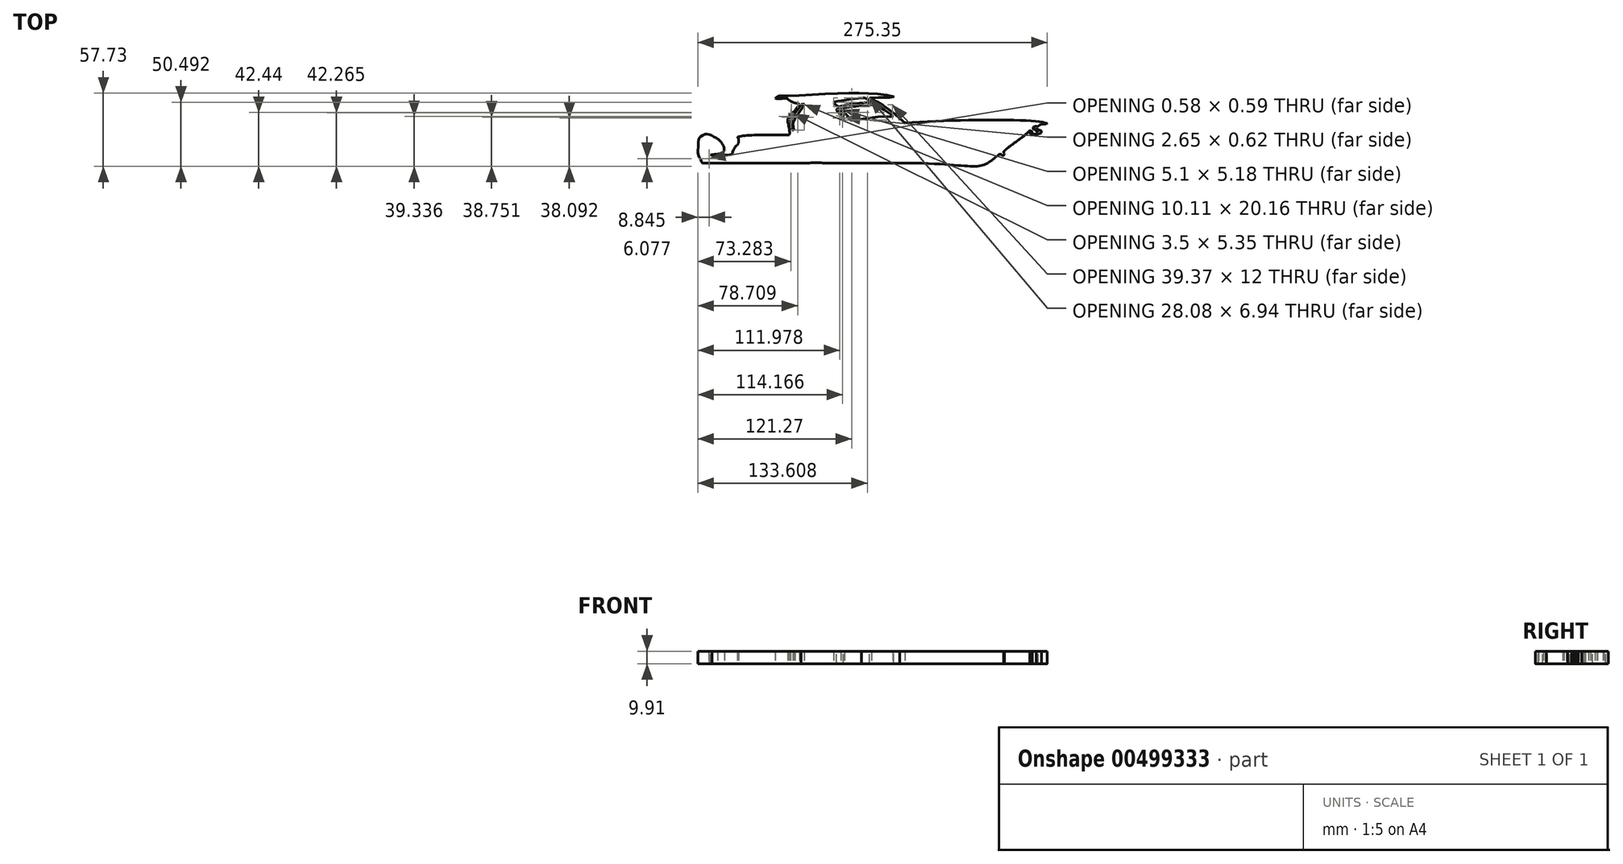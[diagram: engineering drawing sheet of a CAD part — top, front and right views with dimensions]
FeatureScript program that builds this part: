
annotation { "Feature Type Name" : "Feature", "Feature Type Description" : "" }
export const myFeature = defineFeature(function(context is Context, id is Id, definition is map)
    precondition{}
    {
        {
            var Q0;
            Q0=qCreatedBy(makeId("Top.planeOp"),FACE);
            var sketch = newSketch(context, id + "F0", { "sketchPlane" : qUnion([Q0])});
            skFitSpline(sketch, "E0", {"points": [v(181.82, 12.96) * mm, v(177.4, 14.1) * mm, v(69.7, 13.5) * mm, v(25.53, 9.3) * mm, v(19.92, 8.52) * mm], "startDerivative": vector(1.7, -4.6) * mm, "endDerivative": vector(-96.1, -9.77) * mm});
            skFitSpline(sketch, "E1", {"points": [v(19.92, 8.52) * mm, v(11.89, 7.3) * mm, v(0, 4.75) * mm, v(-5.76, 3.64) * mm, v(-21.62, 3.73) * mm, v(-57.86, 3.13) * mm, v(-62.13, 1.85) * mm, v(-60.42, 1.34) * mm, v(-58.8, 1) * mm, v(-52.92, 0.83) * mm, v(-44.65, 0.83) * mm, v(-38.6, 0.91) * mm, v(-28.44, 1) * mm, v(-16.08, 0.83) * mm, v(-10.37, 0.91) * mm, v(-5.5, 0.91) * mm, v(-2.78, 1.42) * mm, v(1.49, 2.79) * mm, v(4.56, 3.64) * mm, v(10.7, 4.66) * mm, v(15.39, 5.6) * mm, v(20.67, 6.46) * mm, v(27.84, 7.48) * mm, v(53.16, 10.3) * mm, v(65.53, 10.8) * mm, v(70.56, 11.23) * mm, v(181.82, 12.96) * mm], "startDerivative": vector(-204.32, -26.46) * mm, "endDerivative": vector(1116.59, 11.05) * mm});
            skFitSpline(sketch, "E2", {"points": [v(150.8, -6.4) * mm, v(136.83, -7.24) * mm, v(77, -11.4) * mm, v(39.07, -13.62) * mm, v(-5.53, -13.97) * mm, v(-32.22, -13.7) * mm, v(-56.7, -13.54) * mm, v(-83.8, -13.7) * mm, v(-84.92, -14.48) * mm, v(-83.04, -15.59) * mm, v(-76.47, -15.59) * mm, v(-57.71, -15.59) * mm, v(-38.53, -16.01) * mm, v(-32.64, -16.01) * mm, v(-7.32, -16.01) * mm, v(12.55, -15.84) * mm, v(72.24, -13.54) * mm, v(94.33, -11.75) * mm, v(106.35, -10.81) * mm, v(150.8, -6.4) * mm]});
            skFitSpline(sketch, "E3", {"points": [v(-62.13, 1.85) * mm, v(-61.49, 0.78) * mm, v(-61.61, -2.84) * mm, v(-63.48, -5.07) * mm, v(-65.9, -9.53) * mm, v(-67.22, -11.64) * mm, v(-83.62, -12) * mm, v(-83.38, -12.3) * mm, v(-83.8, -13.7) * mm], "startDerivative": vector(9.33, -10.43) * mm, "endDerivative": vector(-10.89, -19.72) * mm});
            skFitSpline(sketch, "E4", {"points": [v(-83.62, -12) * mm, v(-73.3, -9.4) * mm, v(-74.45, -2.78) * mm, v(-77.88, 0.76) * mm], "startDerivative": vector(4.15, 3.72) * mm, "endDerivative": vector(-20.22, 12.96) * mm});
            skFitSpline(sketch, "E5", {"points": [v(-77.88, 0.76) * mm, v(-79.82, 1.87) * mm, v(-83.38, 3.86) * mm, v(-86.1, 4.58) * mm, v(-88.98, 3.98) * mm, v(-91.58, 2.29) * mm, v(-92.7, 0.76) * mm, v(-92.95, -2.8) * mm, v(-93.16, -6.9) * mm, v(-93.43, -10.58) * mm, v(-92.18, -13.75) * mm, v(-90.43, -17.3) * mm, v(-89.7, -18.23) * mm, v(-82.47, -18.23) * mm, v(-82.35, -18.23) * mm], "startDerivative": vector(-35.29, 17.01) * mm, "endDerivative": vector(3.35, -0.6) * mm});
            skFitSpline(sketch, "E6", {"points": [v(-84.92, -14.48) * mm, v(-83.04, -16.64) * mm, v(-82.35, -18.23) * mm], "startDerivative": vector(4.12, -3.97) * mm, "endDerivative": vector(0.95, -4.82) * mm});
            skFitSpline(sketch, "E7", {"points": [v(-80.95, 0.76) * mm, v(-88.13, 0.76) * mm, v(-91.05, 1.27) * mm, v(-89.24, 2.99) * mm, v(-80.95, 0.76) * mm]});
            skFitSpline(sketch, "E8", {"points": [v(149.26, -7.8) * mm, v(147.28, -7.83) * mm, v(113.55, -11.96) * mm, v(83.7, -15.93) * mm, v(65.63, -18.23) * mm, v(43.16, -18.23) * mm, v(35.36, -18.23) * mm, v(37.32, -17.46) * mm, v(40.05, -16.74) * mm, v(43.16, -16.7) * mm, v(43.2, -17.38) * mm], "startDerivative": vector(-28.19, 2) * mm, "endDerivative": vector(-7.93, -28.97) * mm});
            skFitSpline(sketch, "E9", {"points": [v(35.36, -18.23) * mm, v(6.92, -18.23) * mm, v(-5.49, -18.23) * mm, v(-12.01, -18.23) * mm, v(-9.45, -17.33) * mm, v(-8.43, -17.16) * mm, v(-5.53, -17.12) * mm], "startDerivative": vector(-93.99, -0.34) * mm, "endDerivative": vector(31.9, 0.18) * mm});
            skFitSpline(sketch, "E10", {"points": [v(-5.53, -17.12) * mm, v(-5.49, -18.23) * mm], "startDerivative": vector(0.04, -1.11) * mm, "endDerivative": vector(0.04, -1.11) * mm});
            skFitSpline(sketch, "E11", {"points": [v(-12.01, -18.23) * mm, v(-82.35, -18.23) * mm], "startDerivative": vector(-70.34, 0) * mm, "endDerivative": vector(-70.34, 0) * mm});
            skFitSpline(sketch, "E12", {"points": [v(-32.53, 32.61) * mm, v(-29.39, 34.74) * mm, v(-27.97, 34.64) * mm, v(-1.6, 35.86) * mm, v(31.66, 36.87) * mm, v(52.65, 35.66) * mm, v(60.76, 33.83) * mm, v(41.9, 33.02) * mm, v(43.22, 32.3) * mm, v(51.33, 27.95) * mm, v(61.47, 20.65) * mm, v(69.7, 13.5) * mm], "startDerivative": vector(69.06, 54.52) * mm, "endDerivative": vector(89.04, -78.05) * mm});
            skFitSpline(sketch, "E13", {"points": [v(-32.53, 32.61) * mm, v(-26.45, 32.61) * mm, v(-23.5, 32.61) * mm, v(-18.94, 29.77) * mm, v(-13.47, 27.98) * mm, v(-16.91, 22.68) * mm], "startDerivative": vector(30.81, -1.19) * mm, "endDerivative": vector(-8.73, -35.9) * mm});
            skFitSpline(sketch, "E14", {"points": [v(-16.91, 22.68) * mm, v(-19.75, 20.65) * mm, v(-22.6, 15.68) * mm, v(-21.98, 11.93) * mm, v(-21.17, 4.73) * mm, v(-21.62, 3.73) * mm], "startDerivative": vector(-14.92, -8.12) * mm, "endDerivative": vector(-5.25, -6.4) * mm});
            skFitSpline(sketch, "E15", {"points": [v(-18.44, 21.16) * mm, v(-20.8, 18.68) * mm, v(-22.04, 16.19) * mm, v(-21.62, 15.68) * mm, v(-20.23, 17.88) * mm, v(-18.44, 21.16) * mm]});
            skFitSpline(sketch, "E16", {"points": [v(-9.7, 27.98) * mm, v(-11.33, 27.98) * mm, v(-20.28, 13.5) * mm, v(-19.94, 11.75) * mm, v(-18.94, 7.75) * mm, v(-17.85, 7.92) * mm, v(-18.44, 11.84) * mm, v(-18.44, 13.5) * mm, v(-16.91, 16.62) * mm, v(-9.96, 27.1) * mm, v(-9.7, 27.98) * mm]});
            skFitSpline(sketch, "E17", {"points": [v(-9.7, 27.98) * mm, v(-5.44, 32.9) * mm, v(-3.74, 33.33) * mm, v(4.36, 33.24) * mm, v(6.07, 32.14) * mm, v(10.59, 28.8) * mm, v(12.12, 27.98) * mm, v(14.77, 25.31) * mm, v(15.8, 24.3) * mm, v(15.53, 23.18) * mm, v(17.58, 21.05) * mm, v(19.97, 19.09) * mm, v(22.19, 18.51) * mm, v(23.9, 16.79) * mm, v(19.37, 17.55) * mm, v(18.43, 16.79) * mm, v(15.36, 14.06) * mm, v(13.06, 12.52) * mm, v(8.46, 11.5) * mm, v(8.54, 10.05) * mm, v(8.37, 7.4) * mm, v(-4.85, 5.62) * mm, v(-5.61, 5.36) * mm], "startDerivative": vector(75.6, 96.22) * mm, "endDerivative": vector(-15.4, -12.16) * mm});
            skFitSpline(sketch, "E18", {"points": [v(-8.77, 17.8) * mm, v(-9.7, 16.87) * mm, v(-5.61, 5.36) * mm], "startDerivative": vector(-4.93, -2.36) * mm, "endDerivative": vector(8.91, -19.64) * mm});
            skFitSpline(sketch, "E19", {"points": [v(1.49, 2.79) * mm, v(10.57, 2.79) * mm, v(29.44, 2.79) * mm, v(48.6, 3.64) * mm, v(74.48, 3.64) * mm, v(166.01, 5.23) * mm], "startDerivative": vector(71.82, 0.39) * mm, "endDerivative": vector(290.97, 6.55) * mm});
            skFitSpline(sketch, "E20", {"points": [v(26.77, 15.59) * mm, v(34.58, 16.15) * mm, v(41.48, 17.07) * mm, v(55.63, 18.51) * mm, v(60.25, 18.51) * mm, v(48.31, 27.11) * mm, v(46.42, 27.9) * mm, v(19.37, 24.28) * mm, v(19.74, 23.5) * mm, v(22.19, 21.5) * mm, v(24.66, 18.51) * mm, v(26.77, 15.59) * mm]});
            skFitSpline(sketch, "E21", {"points": [v(13.76, 29.24) * mm, v(16.86, 26.33) * mm, v(18.89, 26.53) * mm, v(27.64, 28.2) * mm, v(41.98, 29.67) * mm, v(43.34, 30.05) * mm, v(38.46, 33.01) * mm, v(38.1, 33.25) * mm, v(14.63, 29.92) * mm, v(13.76, 29.24) * mm]});
            skFitSpline(sketch, "E22", {"points": [v(-8.77, 17.8) * mm, v(-7.56, 17.8) * mm, v(-6.18, 17.08) * mm, v(-5.74, 15.7) * mm, v(-5.85, 14.54) * mm, v(-5.43, 13.78) * mm, v(-4.73, 12.96) * mm, v(-4.47, 12.29) * mm, v(-4.18, 10.85) * mm, v(-4.5, 10.05) * mm, v(-5.42, 9.95) * mm, v(-5.63, 10.2) * mm, v(-5.48, 9.7) * mm, v(-4.47, 9.56) * mm, v(-4.33, 9.04) * mm, v(-4.55, 8.18) * mm, v(-4.93, 7.57) * mm, v(-4.44, 7.36) * mm, v(-3.33, 7.46) * mm, v(-2.87, 7.5) * mm, v(-2.04, 7.44) * mm, v(-1.18, 7.36) * mm, v(-1.4, 7.87) * mm, v(-1.56, 8.67) * mm, v(-2.61, 8.38) * mm, v(-3.14, 8.38) * mm, v(-3.5, 8.96) * mm, v(-3.95, 9.81) * mm, v(-3.88, 10.36) * mm, v(-3.47, 10.77) * mm, v(-2.85, 11.05) * mm, v(-2.42, 11.23) * mm, v(-2.3, 11.3) * mm, v(-1.62, 11.36) * mm, v(-0.73, 11.34) * mm, v(0, 11.25) * mm, v(0.28, 11.23) * mm, v(0.86, 10.96) * mm, v(1.2, 10.38) * mm, v(1.3, 9.67) * mm, v(1.05, 8.97) * mm, v(0.64, 8.35) * mm, v(-0.37, 8.13) * mm, v(-0.7, 8.7) * mm, v(-0.38, 7.64) * mm, v(0, 7.49) * mm, v(0.33, 7.58) * mm, v(0.9, 7.25) * mm, v(1.24, 6.7) * mm, v(1.16, 5.96) * mm], "startDerivative": vector(43.94, 4.5) * mm, "endDerivative": vector(-8.27, -37.04) * mm});
            skFitSpline(sketch, "E23", {"points": [v(-8.5, 27.45) * mm, v(-4.26, 32.27) * mm, v(2.23, 32.52) * mm, v(4.94, 32.45) * mm, v(7.6, 30.05) * mm, v(9.97, 28) * mm, v(10.6, 27.5) * mm, v(11.35, 27.71) * mm, v(12.43, 26.32) * mm, v(13.95, 24.87) * mm, v(14.8, 23.32) * mm, v(15.48, 21.77) * mm, v(17.68, 19.4) * mm, v(19.91, 18.22) * mm, v(21.15, 17.96) * mm, v(22.02, 17.02) * mm, v(19.37, 17.55) * mm], "startDerivative": vector(33.9, 59.8) * mm, "endDerivative": vector(-58.09, 18.3) * mm});
            skFitSpline(sketch, "E24", {"points": [v(16.21, 24.28) * mm, v(16.2, 22.81) * mm, v(17.02, 21.99) * mm, v(19.65, 19.25) * mm, v(21.28, 19.16) * mm, v(16.21, 24.28) * mm]});
            skFitSpline(sketch, "E25", {"points": [v(135.07, -18.23) * mm, v(65.63, -18.23) * mm], "startDerivative": vector(-70.36, -0.54) * mm, "endDerivative": vector(-70.36, -0.54) * mm});
            skFitSpline(sketch, "E26", {"points": [v(181.82, 12.96) * mm, v(181.8, 12.56) * mm, v(177.64, 12.46) * mm, v(176.2, 11.71) * mm, v(174.48, 10.62) * mm, v(172.8, 10.68) * mm, v(170.42, 9.1) * mm, v(172.64, 8.01) * mm, v(174.17, 8.9) * mm, v(174.76, 8.64) * mm, v(173.59, 7.73) * mm, v(173.23, 7.42) * mm, v(173.27, 6.7) * mm, v(173.5, 6.44) * mm, v(176.84, 7.94) * mm, v(177.07, 5.59) * mm, v(174.73, 4.6) * mm, v(168.22, 4.86) * mm, v(168.71, 5.13) * mm, v(169.93, 5.44) * mm, v(170.02, 6.69) * mm, v(168.84, 7.1) * mm, v(168.39, 7.48) * mm, v(166.01, 5.23) * mm, v(147.56, -9.34) * mm, v(147.8, -10.15) * mm, v(147.89, -11.95) * mm, v(146.26, -12.14) * mm, v(145.13, -11.3) * mm, v(135.07, -18.23) * mm, v(65.63, -18.23) * mm], "startDerivative": vector(13.7, -37.03) * mm, "endDerivative": vector(-923.69, 0) * mm});
            skLineSegment(sketch, "E27", {"start": v(111.62, -18.42) * mm, "end": v(141.39, -13.6) * mm});
            skLineSegment(sketch, "E28", {"start": v(122, -18.29) * mm, "end": v(141.39, -13.6) * mm});
            skSolve(sketch);
        }
        {
            var Q0;
            {var subQ0=sQuery(id+"F0.wireOp",EDGE,"E26");var subQ1=sQuery(id+"F0.wireOp",EDGE,"E25");var subQ2=makeQuery(id+"F0.imprint","INTERSECT",VERTEX,{"derivedFrom":[subQ1,subQ0]});Q0=makeQuery(id+"F0.imprint","IMPRINT",FACE,{"disambiguationData":[TD([[makeQuery(id+"F0.imprint","IMPRINT",EDGE,{"disambiguationData":[TD([[subQ2,-1.0]])],"derivedFrom":subQ1}),1.0]])]});}
            var Q1;
            {var subQ0=sQuery(id+"F0.wireOp",EDGE,"E28");Q1=makeQuery(id+"F0.imprint","IMPRINT",FACE,{"disambiguationData":[TD([[makeQuery(id+"F0.imprint","IMPRINT",EDGE,{"derivedFrom":subQ0}),1.0]])]});}
            var Q2;
            {var subQ3=sQuery(id+"F0.wireOp",EDGE,"E28");Q2=makeQuery(id+"F0.imprint","IMPRINT",FACE,{"disambiguationData":[TD([[makeQuery(id+"F0.imprint","IMPRINT",EDGE,{"derivedFrom":subQ3}),-1.0]])]});}
            var Q3;
            {var subQ0=sQuery(id+"F0.wireOp",EDGE,"E26");var subQ2=sQuery(id+"F0.wireOp",EDGE,"E8");var subQ4=makeQuery(id+"F0.imprint","INTERSECT",VERTEX,{"derivedFrom":[subQ2,subQ0]});Q3=makeQuery(id+"F0.imprint","IMPRINT",FACE,{"disambiguationData":[TD([[makeQuery(id+"F0.imprint","IMPRINT",EDGE,{"disambiguationData":[TD([[subQ4,-1.0]])],"derivedFrom":subQ2}),1.0]])]});}
            var Q4;
            {var subQ1=sQuery(id+"F0.wireOp",EDGE,"E2");var subQ5=makeQuery(id+"F0.imprint","INTERSECT",VERTEX,{"derivedFrom":[subQ1,sQuery(id+"F0.wireOp",EDGE,"E3")]});Q4=makeQuery(id+"F0.imprint","IMPRINT",FACE,{"disambiguationData":[TD([[makeQuery(id+"F0.imprint","IMPRINT",EDGE,{"disambiguationData":[TD([[subQ5,1.0]])],"derivedFrom":subQ1}),1.0]])]});}
            var Q5;
            {var subQ11=sQuery(id+"F0.wireOp",EDGE,"E10");Q5=makeQuery(id+"F0.imprint","IMPRINT",FACE,{"disambiguationData":[TD([[makeQuery(id+"F0.imprint","IMPRINT",EDGE,{"derivedFrom":subQ11}),1.0]])]});}
            var Q6;
            {var subQ0=sQuery(id+"F0.wireOp",EDGE,"E10");Q6=makeQuery(id+"F0.imprint","IMPRINT",FACE,{"disambiguationData":[TD([[makeQuery(id+"F0.imprint","IMPRINT",EDGE,{"derivedFrom":subQ0}),-1.0]])]});}
            var Q7;
            {var subQ8=sQuery(id+"F0.wireOp",EDGE,"E19");Q7=makeQuery(id+"F0.imprint","IMPRINT",FACE,{"disambiguationData":[TD([[makeQuery(id+"F0.imprint","IMPRINT",EDGE,{"derivedFrom":subQ8}),-1.0]])]});}
            var Q8;
            {var subQ3=sQuery(id+"F0.wireOp",EDGE,"E19");Q8=makeQuery(id+"F0.imprint","IMPRINT",FACE,{"disambiguationData":[TD([[makeQuery(id+"F0.imprint","IMPRINT",EDGE,{"derivedFrom":subQ3}),1.0]])]});}
            var Q9;
            {var subQ1=sQuery(id+"F0.wireOp",EDGE,"E1");var subQ4=sQuery(id+"F0.wireOp",EDGE,"E0");var subQ5=makeQuery(id+"F0.imprint","INTERSECT",VERTEX,{"derivedFrom":[subQ4,subQ1]});Q9=makeQuery(id+"F0.imprint","IMPRINT",FACE,{"disambiguationData":[TD([[makeQuery(id+"F0.imprint","IMPRINT",EDGE,{"disambiguationData":[TD([[subQ5,1.0]])],"derivedFrom":subQ4}),1.0]])]});}
            var Q10;
            {var subQ0=sQuery(id+"F0.wireOp",EDGE,"E18");Q10=makeQuery(id+"F0.imprint","IMPRINT",FACE,{"disambiguationData":[TD([[makeQuery(id+"F0.imprint","IMPRINT",EDGE,{"derivedFrom":subQ0}),1.0]])]});}
            var Q11;
            {var subQ0=sQuery(id+"F0.wireOp",EDGE,"E4");Q11=makeQuery(id+"F0.imprint","IMPRINT",FACE,{"disambiguationData":[TD([[makeQuery(id+"F0.imprint","IMPRINT",EDGE,{"derivedFrom":subQ0}),1.0]])]});}
            var Q12;
            Q12=makeQuery(id+"F0.imprint","IMPRINT",FACE,{"disambiguationData":[TD([[makeQuery(id+"F0.imprint","IMPRINT",EDGE,{"derivedFrom":sQuery(id+"F0.wireOp",EDGE,"E7")}),-1.0]])]});
            var Q13;
            {var subQ9=sQuery(id+"F0.wireOp",EDGE,"E12");Q13=makeQuery(id+"F0.imprint","IMPRINT",FACE,{"disambiguationData":[TD([[makeQuery(id+"F0.imprint","IMPRINT",EDGE,{"derivedFrom":subQ9}),-1.0]])]});}
            var Q14;
            {var subQ4=sQuery(id+"F0.wireOp",EDGE,"E0");var subQ7=makeQuery(id+"F0.imprint","INTERSECT",VERTEX,{"derivedFrom":[subQ4,sQuery(id+"F0.wireOp",EDGE,"E12")]});Q14=makeQuery(id+"F0.imprint","IMPRINT",FACE,{"disambiguationData":[TD([[makeQuery(id+"F0.imprint","IMPRINT",EDGE,{"disambiguationData":[TD([[subQ7,1.0]])],"derivedFrom":subQ4}),1.0]])]});}
            extrude(context, id + "F1", {"entities" : qUnion([Q0, Q1, Q2, Q3, Q4, Q5, Q6, Q7, Q8, Q9, Q10, Q11, Q12, Q13, Q14]), "depth" : 9.9 * mm, "offsetDistance" : 25.4 * mm});
        }
    });
